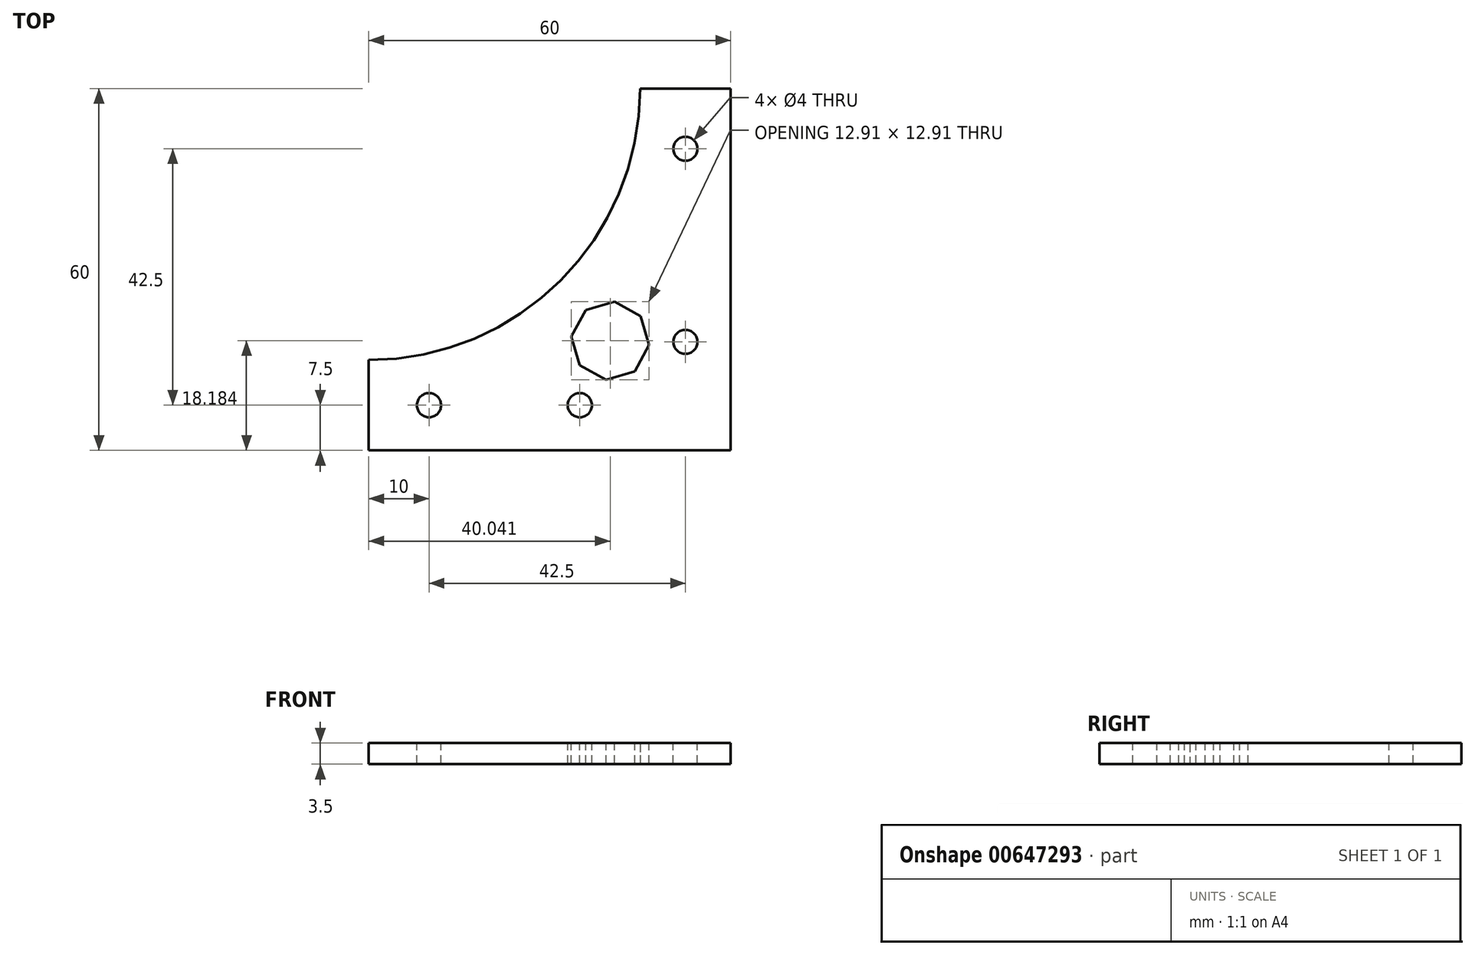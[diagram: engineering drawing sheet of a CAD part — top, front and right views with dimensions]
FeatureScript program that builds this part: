
annotation { "Feature Type Name" : "Feature", "Feature Type Description" : "" }
export const myFeature = defineFeature(function(context is Context, id is Id, definition is map)
    precondition{}
    {
        {
            var Q0;
            Q0=qCreatedBy(makeId("Top.planeOp"),FACE);
            var sketch = newSketch(context, id + "F0", { "sketchPlane" : qUnion([Q0])});
            skLineSegment(sketch, "E0", {"start": v(0, 0) * mm, "end": v(0, 60) * mm});
            skLineSegment(sketch, "E1", {"start": v(0, 0) * mm, "end": v(-60, 0) * mm});
            skLineSegment(sketch, "E2", {"start": v(-60, 0) * mm, "end": v(-60, 15) * mm});
            skLineSegment(sketch, "E3", {"start": v(0, 60) * mm, "end": v(-15, 60) * mm});
            skArc(sketch, "E4", {"start": v(-60, 15) * mm, "mid": v(-28.18, 28.18) * mm, "end": v(-15, 60) * mm});
            skLineSegment(sketch, "E5", {"start": v(0, 0) * mm, "end": v(-30, 0) * mm});
            skSolve(sketch);
        }
        {
            var Q0;
            Q0 = qSketchRegion(id + "F0", true);
            extrude(context, id + "F1", {"entities" : qUnion([Q0]), "depth" : 3.5 * mm, "offsetDistance" : 25 * mm});
        }
        {
            var Q0;
            Q0=makeQuery(id+"F1.opExtrude","CAP_FACE",FACE,{"disambiguationData":[OSD([sQuery(id+"F0.wireOp",EDGE,"E0"),sQuery(id+"F0.wireOp",EDGE,"E1"),sQuery(id+"F0.wireOp",EDGE,"E2"),sQuery(id+"F0.wireOp",EDGE,"E3"),sQuery(id+"F0.wireOp",EDGE,"E4"),sQuery(id+"F0.wireOp",EDGE,"E5")])],"isStart":false});
            var sketch = newSketch(context, id + "F2", { "sketchPlane" : qUnion([Q0])});
            skLineSegment(sketch, "E6", {"start": v(0, 0) * mm, "end": v(-19.96, 18.18) * mm});
            skLineSegment(sketch, "E7", {"start": v(-60, 0) * mm, "end": v(-50, 0) * mm});
            skLineSegment(sketch, "E8", {"start": v(-50, 0) * mm, "end": v(-50, 7.5) * mm});
            skCircle(sketch, "E9", {"center": v(-50, 7.5) * mm, "radius": 2 * mm});
            skLineSegment(sketch, "E10", {"start": v(0, 0) * mm, "end": v(-25, 0) * mm});
            skLineSegment(sketch, "E11", {"start": v(-25, 0) * mm, "end": v(-25, 7.5) * mm});
            skCircle(sketch, "E12", {"center": v(-25, 7.5) * mm, "radius": 2 * mm});
            skLineSegment(sketch, "E13", {"start": v(0, 0) * mm, "end": v(-7.5, 0) * mm});
            skCircle(sketch, "E14", {"center": v(-7.5, 18) * mm, "radius": 2 * mm});
            skLineSegment(sketch, "E15", {"start": v(-7.5, 18) * mm, "end": v(-7.5, 20) * mm});
            skLineSegment(sketch, "E16", {"start": v(-7.5, 52) * mm, "end": v(-7.5, 50) * mm});
            skCircle(sketch, "E17", {"center": v(-7.5, 50) * mm, "radius": 2 * mm});
            skLineSegment(sketch, "E18.trimOffspring", {"start": v(-7.5, 48) * mm, "end": v(-7.5, 60) * mm});
            skLineSegment(sketch, "E19.trimOffspring", {"start": v(-7.5, 16) * mm, "end": v(-7.5, 18) * mm});
            skCircle(sketch, "E20.cCircle", {"center": v(-19.96, 18.18) * mm, "radius": 6 * mm, "construction": true});
            skLineSegment(sketch, "E20.0", {"start": v(-19.26, 24.64) * mm, "end": v(-14.9, 22.26) * mm});
            skLineSegment(sketch, "E20.1", {"start": v(-14.9, 22.26) * mm, "end": v(-13.5, 17.49) * mm});
            skLineSegment(sketch, "E20.2", {"start": v(-13.5, 17.49) * mm, "end": v(-15.89, 13.13) * mm});
            skLineSegment(sketch, "E20.3", {"start": v(-15.89, 13.13) * mm, "end": v(-20.66, 11.73) * mm});
            skLineSegment(sketch, "E20.4", {"start": v(-20.66, 11.73) * mm, "end": v(-25.02, 14.11) * mm});
            skLineSegment(sketch, "E20.5", {"start": v(-25.02, 14.11) * mm, "end": v(-26.42, 18.88) * mm});
            skLineSegment(sketch, "E20.6", {"start": v(-26.42, 18.88) * mm, "end": v(-24.03, 23.24) * mm});
            skLineSegment(sketch, "E20.7", {"start": v(-24.03, 23.24) * mm, "end": v(-19.26, 24.64) * mm});
            skPoint(sketch, "E20.0.midPoint", {"position": v(-17.08, 23.45) * mm});
            skSolve(sketch);
        }
        {
            var Q0;
            Q0 = qSketchRegion(id + "F2", true);
            extrude(context, id + "F3", {"entities" : qUnion([Q0]), "operationType" : NewBodyOperationType.REMOVE, "oppositeDirection" : true, "depth" : 25 * mm, "offsetDistance" : 25 * mm});
        }
    });
